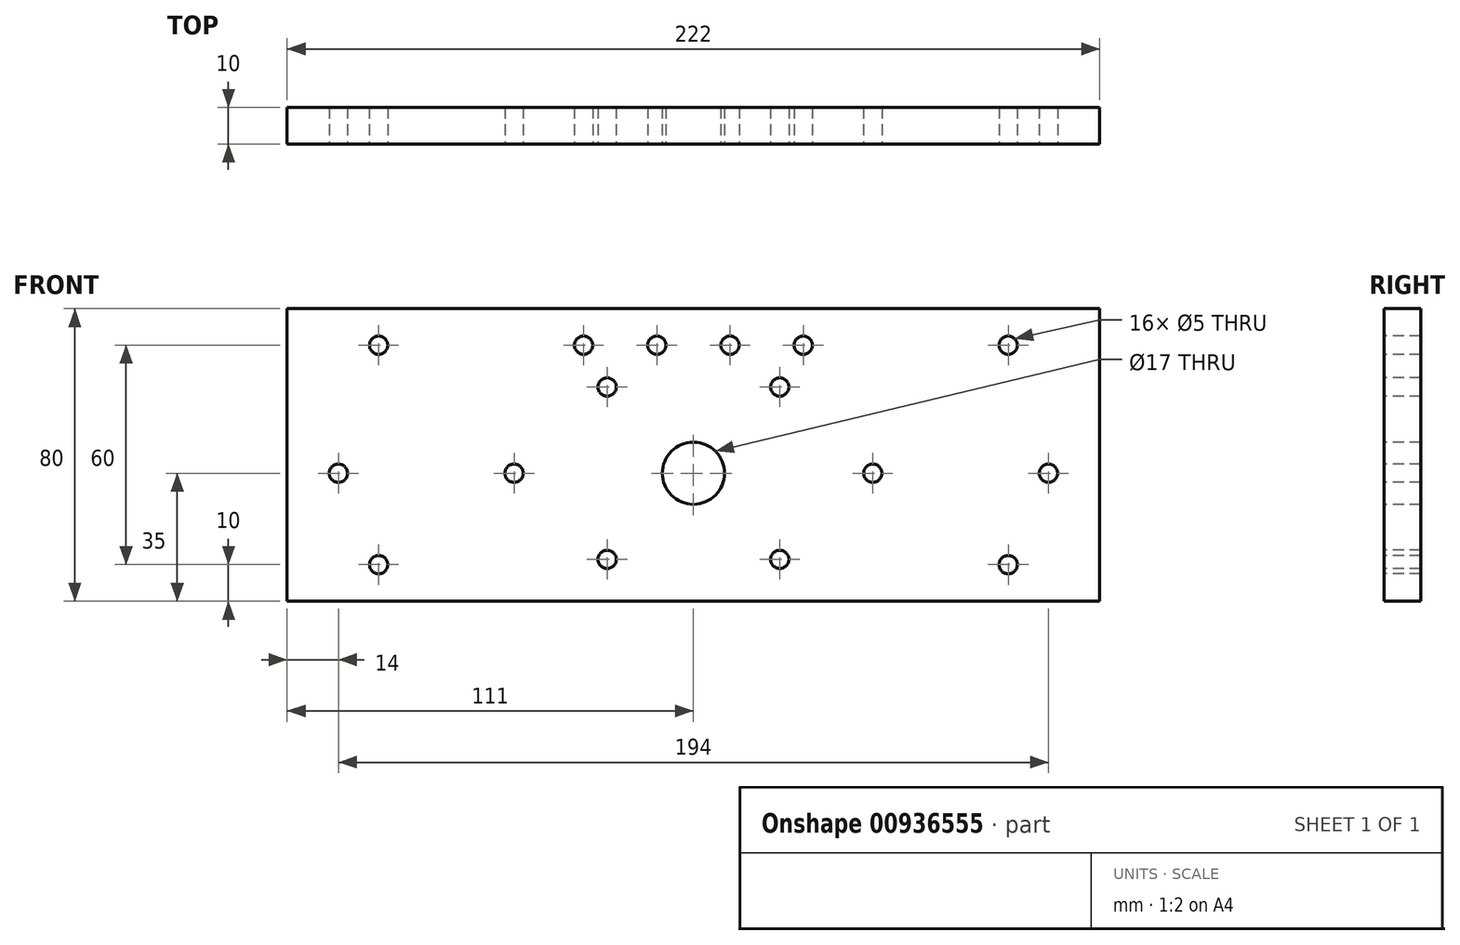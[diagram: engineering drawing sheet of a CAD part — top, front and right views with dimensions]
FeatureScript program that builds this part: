
annotation { "Feature Type Name" : "Feature", "Feature Type Description" : "" }
export const myFeature = defineFeature(function(context is Context, id is Id, definition is map)
    precondition{}
    {
        {
            var Q0;
            Q0=qCreatedBy(makeId("Front.planeOp"),FACE);
            var sketch = newSketch(context, id + "F0", { "sketchPlane" : qUnion([Q0])});
            skLineSegment(sketch, "E0.bottom", {"start": v(111, 40) * mm, "end": v(-111, 40) * mm});
            skLineSegment(sketch, "E0.top", {"start": v(111, -40) * mm, "end": v(-111, -40) * mm});
            skLineSegment(sketch, "E0.left", {"start": v(111, 40) * mm, "end": v(111, -40) * mm});
            skLineSegment(sketch, "E0.right", {"start": v(-111, 40) * mm, "end": v(-111, -40) * mm});
            skPoint(sketch, "E0.middle", {"position": v(0, 0) * mm});
            skPoint(sketch, "E1", {"position": v(-73, -5) * mm});
            skPoint(sketch, "E2.MirrorP", {"position": v(73, -5) * mm});
            skLineSegment(sketch, "E3", {"start": v(-73, -5) * mm, "end": v(-73, 30.44) * mm, "construction": true});
            skLineSegment(sketch, "E4", {"start": v(73, -5) * mm, "end": v(73, 28.61) * mm, "construction": true});
            skPoint(sketch, "E5", {"position": v(49, -5) * mm});
            skPoint(sketch, "E6", {"position": v(97, -5) * mm});
            skPoint(sketch, "E7", {"position": v(-49, -5) * mm});
            skPoint(sketch, "E8", {"position": v(-97, -5) * mm});
            skPoint(sketch, "E9", {"position": v(0, -5) * mm});
            skPoint(sketch, "E10", {"position": v(86, -30) * mm});
            skPoint(sketch, "E11", {"position": v(86, 30) * mm});
            skPoint(sketch, "E12.MirrorP", {"position": v(-86, 30) * mm});
            skPoint(sketch, "E13.MirrorP", {"position": v(-86, -30) * mm});
            skLineSegment(sketch, "E14", {"start": v(-86, 30) * mm, "end": v(86, 30) * mm, "construction": true});
            skPoint(sketch, "E15", {"position": v(-10, 30) * mm});
            skPoint(sketch, "E16", {"position": v(-30, 30) * mm});
            skPoint(sketch, "E17.MirrorP", {"position": v(10, 30) * mm});
            skPoint(sketch, "E18.MirrorP", {"position": v(30, 30) * mm});
            skCircle(sketch, "E19", {"center": v(0, -5) * mm, "radius": 33.33 * mm, "construction": true});
            skLineSegment(sketch, "E20", {"start": v(0, -5) * mm, "end": v(-24.25, 19.25) * mm, "construction": true});
            skPoint(sketch, "E21", {"position": v(-23.57, 18.57) * mm});
            skPoint(sketch, "E22.MirrorP", {"position": v(23.57, 18.57) * mm});
            skLineSegment(sketch, "E23", {"start": v(0, -5) * mm, "end": v(33.33, -5) * mm, "construction": true});
            skPoint(sketch, "E24.MirrorP", {"position": v(23.57, -28.57) * mm});
            skPoint(sketch, "E25.MirrorP", {"position": v(-23.57, -28.57) * mm});
            skSolve(sketch);
        }
        {
            var Q0;
            Q0=makeQuery(id+"F0.imprint","IMPRINT",FACE,{"disambiguationData":[TD([[makeQuery(id+"F0.imprint","IMPRINT",EDGE,{"derivedFrom":sQuery(id+"F0.wireOp",EDGE,"E0.bottom")}),1.0]])]});
            extrude(context, id + "F1", {"entities" : qUnion([Q0]), "depth" : 10 * mm, "offsetDistance" : 25 * mm});
        }
        {
            var Q0;
            Q0=sQuery(id+"F0.wireOp",VERTEX,"E6");
            var Q1;
            Q1=sQuery(id+"F0.wireOp",VERTEX,"E5");
            var Q2;
            Q2=sQuery(id+"F0.wireOp",VERTEX,"E7");
            var Q3;
            Q3=sQuery(id+"F0.wireOp",VERTEX,"E8");
            var Q4;
            Q4=makeQuery(id+"F1.opExtrude","SWEPT_BODY",BODY,{"disambiguationData":[OSD([sQuery(id+"F0.wireOp",EDGE,"E0.bottom"),sQuery(id+"F0.wireOp",EDGE,"E0.top"),sQuery(id+"F0.wireOp",EDGE,"E0.left"),sQuery(id+"F0.wireOp",EDGE,"E0.right")])]});
            hole(context, id + "F2", {"style" : HoleStyle.SIMPLE, "endStyle" : HoleEndStyle.THROUGH, "oppositeDirection" : true, "standardTappedOrClearance" : lookupTablePath({ "standard" : "ISO", "engagement" : "75%", "pitch" : "1 mm", "size" : "M6", "type" : "Tapped" }), "standardBlindInLast" : lookupTablePath({ "standard" : "ISO", "engagement" : "75%", "pitch" : "1 mm", "size" : "M6", "type" : "Tapped" }), "holeDiameter" : 5 * mm, "majorDiameter" : 6 * mm, "showTappedDepth" : true, "tappedDepth" : 12 * mm, "tapClearance" : 3, "locations" : qUnion([Q0, Q1, Q2, Q3]), "scope" : qUnion([Q4]), "startStyle" : HoleStartStyle.PART});
        }
        {
            var Q0;
            Q0=sQuery(id+"F0.wireOp",VERTEX,"E9");
            var Q1;
            Q1=makeQuery(id+"F1.opExtrude","SWEPT_BODY",BODY,{"disambiguationData":[OSD([sQuery(id+"F0.wireOp",EDGE,"E0.bottom"),sQuery(id+"F0.wireOp",EDGE,"E0.top"),sQuery(id+"F0.wireOp",EDGE,"E0.left"),sQuery(id+"F0.wireOp",EDGE,"E0.right")])]});
            hole(context, id + "F3", {"style" : HoleStyle.SIMPLE, "endStyle" : HoleEndStyle.THROUGH, "oppositeDirection" : true, "standardTappedOrClearance" : lookupTablePath({ "standard" : "ISO", "size" : "17", "type" : "Drilled" }), "standardBlindInLast" : lookupTablePath({ "standard" : "ISO", "size" : "17", "type" : "Drilled" }), "holeDiameter" : 17 * mm, "majorDiameter" : 4 * mm, "tappedDepth" : 12 * mm, "tapClearance" : 3, "locations" : qUnion([Q0]), "scope" : qUnion([Q1]), "startStyle" : HoleStartStyle.PART});
        }
        {
            var Q0;
            Q0=sQuery(id+"F0.wireOp",VERTEX,"E12.MirrorP");
            var Q1;
            Q1=sQuery(id+"F0.wireOp",VERTEX,"E13.MirrorP");
            var Q2;
            Q2=sQuery(id+"F0.wireOp",VERTEX,"E10");
            var Q3;
            Q3=sQuery(id+"F0.wireOp",VERTEX,"E11");
            var Q4;
            Q4=makeQuery(id+"F1.opExtrude","SWEPT_BODY",BODY,{"disambiguationData":[OSD([sQuery(id+"F0.wireOp",EDGE,"E0.bottom"),sQuery(id+"F0.wireOp",EDGE,"E0.top"),sQuery(id+"F0.wireOp",EDGE,"E0.left"),sQuery(id+"F0.wireOp",EDGE,"E0.right")])]});
            hole(context, id + "F4", {"style" : HoleStyle.SIMPLE, "endStyle" : HoleEndStyle.THROUGH, "oppositeDirection" : true, "standardTappedOrClearance" : lookupTablePath({ "standard" : "ISO", "size" : "5", "type" : "Drilled" }), "standardBlindInLast" : lookupTablePath({ "standard" : "ISO", "size" : "5", "type" : "Drilled" }), "holeDiameter" : 5 * mm, "majorDiameter" : 5 * mm, "tappedDepth" : 12 * mm, "tapClearance" : 3, "locations" : qUnion([Q0, Q1, Q2, Q3]), "scope" : qUnion([Q4]), "startStyle" : HoleStartStyle.PART});
        }
        {
            var Q0;
            Q0=sQuery(id+"F0.wireOp",VERTEX,"E16");
            var Q1;
            Q1=sQuery(id+"F0.wireOp",VERTEX,"E15");
            var Q2;
            Q2=sQuery(id+"F0.wireOp",VERTEX,"E17.MirrorP");
            var Q3;
            Q3=sQuery(id+"F0.wireOp",VERTEX,"E18.MirrorP");
            var Q4;
            Q4=makeQuery(id+"F1.opExtrude","SWEPT_BODY",BODY,{"disambiguationData":[OSD([sQuery(id+"F0.wireOp",EDGE,"E0.bottom"),sQuery(id+"F0.wireOp",EDGE,"E0.top"),sQuery(id+"F0.wireOp",EDGE,"E0.left"),sQuery(id+"F0.wireOp",EDGE,"E0.right")])]});
            hole(context, id + "F5", {"style" : HoleStyle.SIMPLE, "endStyle" : HoleEndStyle.THROUGH, "oppositeDirection" : true, "standardTappedOrClearance" : lookupTablePath({ "standard" : "ISO", "size" : "5", "type" : "Drilled" }), "standardBlindInLast" : lookupTablePath({ "standard" : "ISO", "size" : "5", "type" : "Drilled" }), "holeDiameter" : 5 * mm, "majorDiameter" : 5 * mm, "tappedDepth" : 12 * mm, "tapClearance" : 3, "locations" : qUnion([Q0, Q1, Q2, Q3]), "scope" : qUnion([Q4]), "startStyle" : HoleStartStyle.PART});
        }
        {
            var Q0;
            Q0=sQuery(id+"F0.wireOp",VERTEX,"E21");
            var Q1;
            Q1=sQuery(id+"F0.wireOp",VERTEX,"E22.MirrorP");
            var Q2;
            Q2=sQuery(id+"F0.wireOp",VERTEX,"E24.MirrorP");
            var Q3;
            Q3=sQuery(id+"F0.wireOp",VERTEX,"E25.MirrorP");
            var Q4;
            Q4=makeQuery(id+"F1.opExtrude","SWEPT_BODY",BODY,{"disambiguationData":[OSD([sQuery(id+"F0.wireOp",EDGE,"E0.bottom"),sQuery(id+"F0.wireOp",EDGE,"E0.top"),sQuery(id+"F0.wireOp",EDGE,"E0.left"),sQuery(id+"F0.wireOp",EDGE,"E0.right")])]});
            hole(context, id + "F6", {"style" : HoleStyle.SIMPLE, "endStyle" : HoleEndStyle.THROUGH, "oppositeDirection" : true, "standardTappedOrClearance" : lookupTablePath({ "standard" : "ISO", "size" : "5", "type" : "Drilled" }), "standardBlindInLast" : lookupTablePath({ "standard" : "ISO", "size" : "5", "type" : "Drilled" }), "holeDiameter" : 5 * mm, "majorDiameter" : 5 * mm, "tappedDepth" : 12 * mm, "tapClearance" : 3, "locations" : qUnion([Q0, Q1, Q2, Q3]), "scope" : qUnion([Q4]), "startStyle" : HoleStartStyle.PART});
        }
    });
